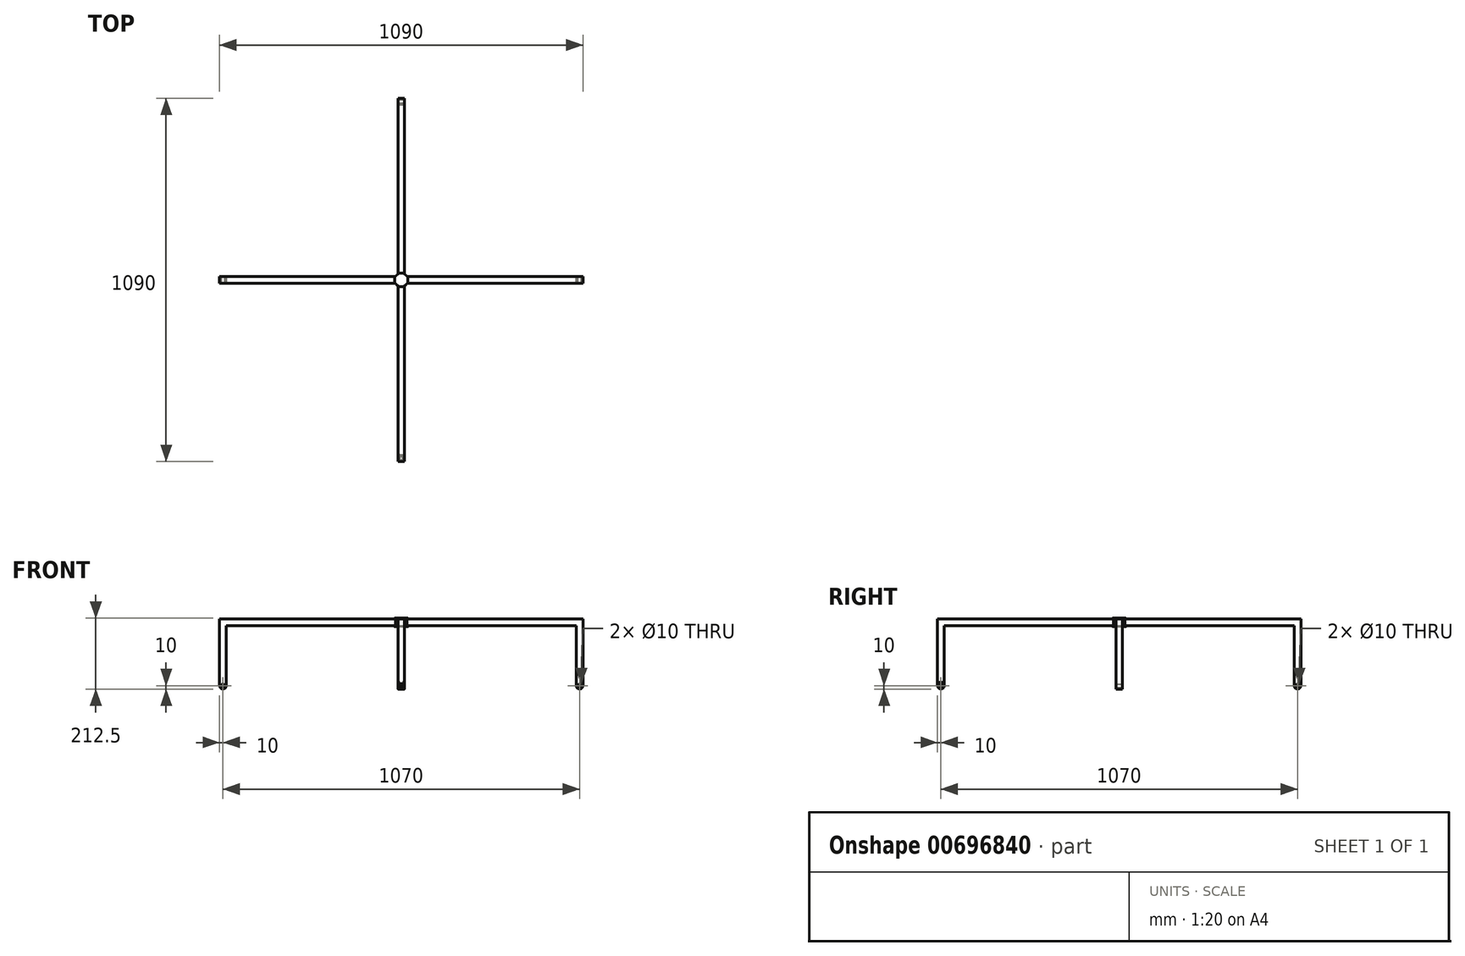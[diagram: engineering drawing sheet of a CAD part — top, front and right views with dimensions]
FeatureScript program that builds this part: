
annotation { "Feature Type Name" : "Feature", "Feature Type Description" : "" }
export const myFeature = defineFeature(function(context is Context, id is Id, definition is map)
    precondition{}
    {
        {
            var Q0;
            Q0=qCreatedBy(makeId("Front.planeOp"),FACE);
            var sketch = newSketch(context, id + "F0", { "sketchPlane" : qUnion([Q0])});
            skLineSegment(sketch, "E0", {"start": v(0, 0) * mm, "end": v(0, 25) * mm});
            skLineSegment(sketch, "E1", {"start": v(0, 25) * mm, "end": v(20, 25) * mm});
            skLineSegment(sketch, "E2", {"start": v(20, 25) * mm, "end": v(20, 22.5) * mm});
            skLineSegment(sketch, "E3", {"start": v(20, 22.5) * mm, "end": v(545, 22.5) * mm});
            skLineSegment(sketch, "E4", {"start": v(545, 22.5) * mm, "end": v(545, -177.5) * mm});
            skLineSegment(sketch, "E5", {"start": v(525, -177.5) * mm, "end": v(525, 2.5) * mm});
            skLineSegment(sketch, "E6", {"start": v(0, 0) * mm, "end": v(20, 0) * mm});
            skLineSegment(sketch, "E7", {"start": v(20, 0) * mm, "end": v(20, 2.5) * mm});
            skLineSegment(sketch, "E8", {"start": v(20, 2.5) * mm, "end": v(525, 2.5) * mm});
            skArc(sketch, "E9", {"start": v(525, -177.5) * mm, "mid": v(535, -187.5) * mm, "end": v(545, -177.5) * mm});
            skCircle(sketch, "E10", {"center": v(535, -177.5) * mm, "radius": 5 * mm});
            skSolve(sketch);
        }
        {
            var Q0;
            Q0=makeQuery(id+"F0.imprint","IMPRINT",FACE,{"disambiguationData":[TD([[makeQuery(id+"F0.imprint","IMPRINT",EDGE,{"derivedFrom":sQuery(id+"F0.wireOp",EDGE,"E0")}),-1.0]])]});
            extrude(context, id + "F1", {"entities" : qUnion([Q0]), "depth" : 20 * mm, "offsetDistance" : 25 * mm});
        }
        {
            var Q0;
            Q0=makeQuery(id+"F1.opExtrude","SWEPT_EDGE",EDGE,{"disambiguationData":[OSD([sQuery(id+"F0.wireOp",EDGE,"E2"),sQuery(id+"F0.wireOp",EDGE,"E3")])]});
            var Q1;
            Q1=makeQuery(id+"F1.opExtrude","SWEPT_EDGE",EDGE,{"disambiguationData":[OSD([sQuery(id+"F0.wireOp",EDGE,"E7"),sQuery(id+"F0.wireOp",EDGE,"E8")])]});
            fillet(context, id + "F2", {"entities" : qUnion([Q0, Q1]), "radius" : 5 * mm, "tangentPropagation" : true, "allowEdgeOverflow" : false});
        }
        {
            var Q0;
            Q0=makeQuery(id+"F1.opExtrude","SWEPT_FACE",FACE,{"disambiguationData":[OSD([sQuery(id+"F0.wireOp",EDGE,"E1")])]});
            var sketch = newSketch(context, id + "F3", { "sketchPlane" : qUnion([Q0])});
            skCircle(sketch, "E11", {"center": v(0, -10) * mm, "radius": 20 * mm});
            skSolve(sketch);
        }
        {
            var Q0;
            Q0=makeQuery(id+"F1.opExtrude","SWEPT_BODY",BODY,{"disambiguationData":[OSD([sQuery(id+"F0.wireOp",EDGE,"E0"),sQuery(id+"F0.wireOp",EDGE,"E1"),sQuery(id+"F0.wireOp",EDGE,"E2"),sQuery(id+"F0.wireOp",EDGE,"E3"),sQuery(id+"F0.wireOp",EDGE,"E4"),sQuery(id+"F0.wireOp",EDGE,"E5"),sQuery(id+"F0.wireOp",EDGE,"E6"),sQuery(id+"F0.wireOp",EDGE,"E7"),sQuery(id+"F0.wireOp",EDGE,"E8"),sQuery(id+"F0.wireOp",EDGE,"E9"),sQuery(id+"F0.wireOp",EDGE,"E10")])]});
            var Q1;
            Q1=sQuery(id+"F3.wireOp",EDGE,"E11");
            circularPattern(context, id + "F4", {"operationType" : NewBodyOperationType.ADD, "entities" : qUnion([Q0]), "axis" : qUnion([Q1]), "angle" : 360 * degree, "instanceCount" : 4, "equalSpace" : true});
        }
        {
            var Q0;
            Q0 = qSketchRegion(id + "F3", true);
            var Q1;
            {var subQ0=makeQuery(id+"F1.opExtrude","SWEPT_FACE",FACE,{"disambiguationData":[OSD([sQuery(id+"F0.wireOp",EDGE,"E6")])]});Q1=makeQuery(id+"F4.boolean.opBoolean","MERGE",FACE,{"derivedFrom":[subQ0,makeQuery(id+"F4.opPattern","COPY",FACE,{"derivedFrom":subQ0,"instanceName":"1"}),makeQuery(id+"F4.opPattern","COPY",FACE,{"derivedFrom":subQ0,"instanceName":"2"}),makeQuery(id+"F4.opPattern","COPY",FACE,{"derivedFrom":subQ0,"instanceName":"3"})]});}
            extrude(context, id + "F5", {"entities" : qUnion([Q0]), "operationType" : NewBodyOperationType.ADD, "endBound" : BoundingType.UP_TO_SURFACE, "oppositeDirection" : true, "depth" : 25 * mm, "endBoundEntityFace" : qUnion([Q1]), "offsetDistance" : 25 * mm});
        }
        {
            var Q0;
            Q0=makeQuery(id+"F4.opPattern","COPY",FACE,{"derivedFrom":makeQuery(id+"F1.opExtrude","CAP_FACE",FACE,{"disambiguationData":[OSD([sQuery(id+"F0.wireOp",EDGE,"E0"),sQuery(id+"F0.wireOp",EDGE,"E1"),sQuery(id+"F0.wireOp",EDGE,"E2"),sQuery(id+"F0.wireOp",EDGE,"E3"),sQuery(id+"F0.wireOp",EDGE,"E4"),sQuery(id+"F0.wireOp",EDGE,"E5"),sQuery(id+"F0.wireOp",EDGE,"E6"),sQuery(id+"F0.wireOp",EDGE,"E7"),sQuery(id+"F0.wireOp",EDGE,"E8"),sQuery(id+"F0.wireOp",EDGE,"E9"),sQuery(id+"F0.wireOp",EDGE,"E10")])],"isStart":false}),"instanceName":"3"});
            var sketch = newSketch(context, id + "F6", { "sketchPlane" : qUnion([Q0])});
            skLineSegment(sketch, "E12.bottom", {"start": v(555, -167.5) * mm, "end": v(535, -167.5) * mm});
            skLineSegment(sketch, "E12.top", {"start": v(555, -187.5) * mm, "end": v(535, -187.5) * mm});
            skLineSegment(sketch, "E12.left", {"start": v(555, -167.5) * mm, "end": v(555, -187.5) * mm});
            skLineSegment(sketch, "E12.right", {"start": v(535, -167.5) * mm, "end": v(535, -187.5) * mm});
            skPoint(sketch, "E12.middle", {"position": v(545, -177.5) * mm});
            skSolve(sketch);
        }
        {
            var Q0;
            {var subQ3=sQuery(id+"F6.wireOp",EDGE,"E12.bottom");Q0=makeQuery(id+"F6.imprint","IMPRINT",FACE,{"disambiguationData":[TD([[makeQuery(id+"F6.imprint","IMPRINT",EDGE,{"derivedFrom":subQ3}),1.0]])]});}
            extrude(context, id + "F7", {"entities" : qUnion([Q0]), "operationType" : NewBodyOperationType.REMOVE, "oppositeDirection" : true, "depth" : 5 * mm, "offsetDistance" : 25 * mm});
        }
        {
            var Q0;
            {var subQ0=sQuery(id+"F0.wireOp",EDGE,"E10");var subQ1=sQuery(id+"F0.wireOp",EDGE,"E9");var subQ2=sQuery(id+"F0.wireOp",EDGE,"E8");var subQ3=sQuery(id+"F0.wireOp",EDGE,"E7");var subQ4=sQuery(id+"F0.wireOp",EDGE,"E6");var subQ5=sQuery(id+"F0.wireOp",EDGE,"E5");var subQ6=sQuery(id+"F0.wireOp",EDGE,"E4");var subQ7=sQuery(id+"F0.wireOp",EDGE,"E3");var subQ8=sQuery(id+"F0.wireOp",EDGE,"E2");var subQ9=sQuery(id+"F0.wireOp",EDGE,"E1");var subQ10=sQuery(id+"F0.wireOp",EDGE,"E0");Q0=makeQuery(id+"F4.boolean.opBoolean","MERGE",FACE,{"disambiguationData":[OD(1.0)],"derivedFrom":[makeQuery(id+"F4.opPattern","COPY",FACE,{"derivedFrom":makeQuery(id+"F1.opExtrude","CAP_FACE",FACE,{"disambiguationData":[OSD([subQ10,subQ9,subQ8,subQ7,subQ6,subQ5,subQ4,subQ3,subQ2,subQ1,subQ0])],"isStart":false}),"instanceName":"1"}),makeQuery(id+"F4.opPattern","COPY",FACE,{"derivedFrom":makeQuery(id+"F1.opExtrude","CAP_FACE",FACE,{"disambiguationData":[OSD([subQ10,subQ9,subQ8,subQ7,subQ6,subQ5,subQ4,subQ3,subQ2,subQ1,subQ0])],"isStart":true}),"instanceName":"3"})]});}
            var sketch = newSketch(context, id + "F8", { "sketchPlane" : qUnion([Q0])});
            skLineSegment(sketch, "E13.bottom", {"start": v(-535, -167.5) * mm, "end": v(-555, -167.5) * mm});
            skLineSegment(sketch, "E13.top", {"start": v(-535, -187.5) * mm, "end": v(-555, -187.5) * mm});
            skLineSegment(sketch, "E13.left", {"start": v(-535, -167.5) * mm, "end": v(-535, -187.5) * mm});
            skLineSegment(sketch, "E13.right", {"start": v(-555, -167.5) * mm, "end": v(-555, -187.5) * mm});
            skPoint(sketch, "E13.middle", {"position": v(-545, -177.5) * mm});
            skSolve(sketch);
        }
        {
            var Q0;
            {var subQ3=sQuery(id+"F8.wireOp",EDGE,"E13.bottom");Q0=makeQuery(id+"F8.imprint","IMPRINT",FACE,{"disambiguationData":[TD([[makeQuery(id+"F8.imprint","IMPRINT",EDGE,{"derivedFrom":subQ3}),1.0]])]});}
            extrude(context, id + "F9", {"entities" : qUnion([Q0]), "operationType" : NewBodyOperationType.REMOVE, "oppositeDirection" : true, "depth" : 5 * mm, "offsetDistance" : 25 * mm});
        }
    });
